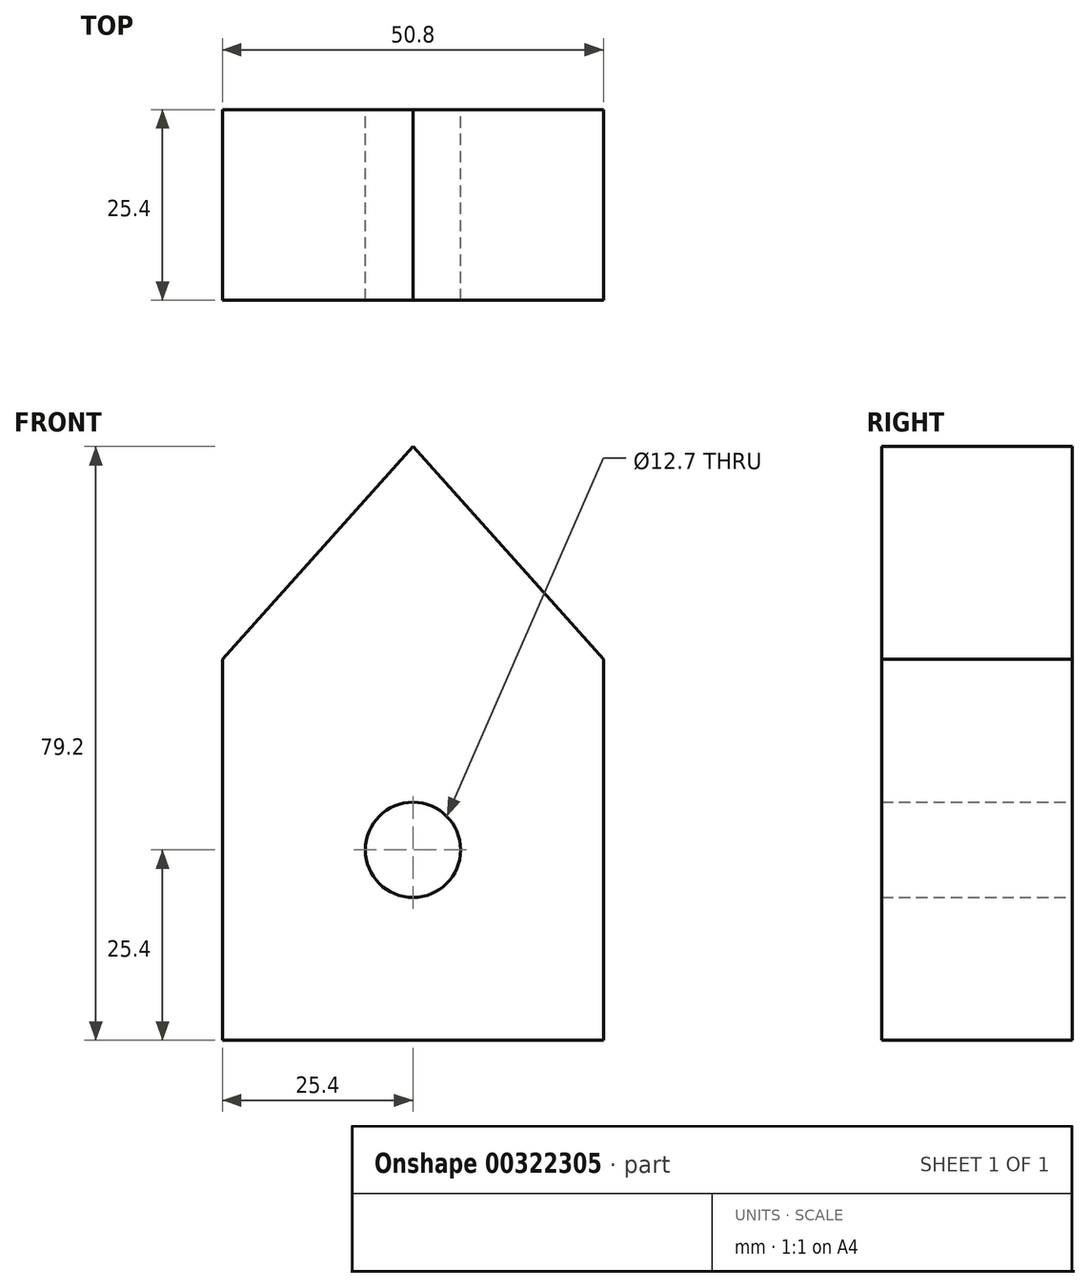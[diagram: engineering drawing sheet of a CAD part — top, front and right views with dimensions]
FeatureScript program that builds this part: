
annotation { "Feature Type Name" : "Feature", "Feature Type Description" : "" }
export const myFeature = defineFeature(function(context is Context, id is Id, definition is map)
    precondition{}
    {
        {
            var Q0;
            Q0=qCreatedBy(makeId("Front.planeOp"),FACE);
            var sketch = newSketch(context, id + "F0", { "sketchPlane" : qUnion([Q0])});
            skLineSegment(sketch, "E0.bottom", {"start": v(-25.4, -25.4) * mm, "end": v(25.4, -25.4) * mm});
            skLineSegment(sketch, "E0.left", {"start": v(-25.4, -25.4) * mm, "end": v(-25.4, 25.4) * mm});
            skLineSegment(sketch, "E0.right", {"start": v(25.4, -25.4) * mm, "end": v(25.4, 25.4) * mm});
            skPoint(sketch, "E0.middle", {"position": v(0, 0) * mm});
            skLineSegment(sketch, "E1", {"start": v(-25.4, 25.4) * mm, "end": v(0, 53.8) * mm});
            skLineSegment(sketch, "E2", {"start": v(25.4, 25.4) * mm, "end": v(0, 53.8) * mm});
            skCircle(sketch, "E3", {"center": v(0, 0) * mm, "radius": 6.35 * mm});
            skSolve(sketch);
        }
        {
            var Q0;
            Q0=makeQuery(id+"F0.imprint","IMPRINT",FACE,{"disambiguationData":[TD([[makeQuery(id+"F0.imprint","IMPRINT",EDGE,{"derivedFrom":sQuery(id+"F0.wireOp",EDGE,"E0.bottom")}),1.0]])]});
            extrude(context, id + "F1", {"entities" : qUnion([Q0]), "depth" : 25.4 * mm});
        }
    });
